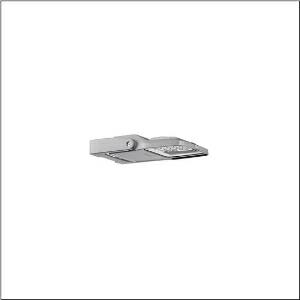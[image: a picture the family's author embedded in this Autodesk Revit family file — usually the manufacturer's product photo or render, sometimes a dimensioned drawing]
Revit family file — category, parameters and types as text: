
# Revit family: floodlight_fl_21_micro___pl52_5xa7761a4d2a_ddfa
name_source: partatom
category: Lighting Fixtures
units: mm (PartAtom-declared; Revit-internal decimal feet)

## family parameters
Cut with Voids When Loaded = No
Host = Face
Light Source = No
Part Type = Normal
Room Calculation Point = No
Round Connector Dimension = Use Diameter
Shared = No

## types (1)
- --- (1 x LED, 3010 lm, 23.1 W, 4000K)
    Apparent Load = 23 VA
    CIE Flux Codes = 26 60 98 100 100
    Color Rendering = 70
    Color Temperature = 4000K
    Default Elevation = 1800 mm
    Description = Floodlight FL 21 micro, floodlight, primary light control with lens, of PMMA, primary optical cover: protective disc, of toughened safety glass, transparent, light distribution: PL52, light emission: direct distribution, installation type: surface-mounted, LED, High Power LED, rated luminous flux: 3.010lm, luminous efficacy: 130lm/W, light colour: 740, colour temperature: 4000K, control gear: ECG iQ, control: optimised constant luminous flux control (CLO 2.0), Desk-Remote (wireless, voltage-free reading and setting of iQ features in the workshop via application-optimized NFC function/RFID function), Light-Fading, Smart-Wire, Night-Set, Lumen-Switch, Temp-Guard, Auto-Match, with terminal, 6-pole, mains connection: 220..240V, AC, 50/60Hz, start of lifetime: 23W, end of lifetime: 24W, reduction: 11W, luminaire housing, of diecast aluminium, powder-coated, Siteco® metallic grey (DB 702S), corrosivity category C5 according to DIN EN ISO 12944, design bracket, of diecast aluminium, powder-coated, Siteco® metallic grey (DB 702S), protection rating (complete): IP66, insulation class (complete): insulation class II (safety insulation), certification: CE, protection symbol: D, impact resistance: IK07, permissible operating ambient temperature: -40..+40°C, permissible operating ambient temperature for outdoor applications: -40..+50°C, standard: DIN EN 12944, packaging unit: 1 piece

Light Distribution: PL52
    Height = 65 mm
    Lamp = 1 x LED
    Lamp Light Flux = 3010 lm
    Lamp Power = 23.1 W
    Lamp count = 1
    Length = 312 mm
    Luminous efficacy = 130 lm/W
    Manufacturer = Siteco
    ModVariant = No
    Model = 5XA7761A4D2A
    Number of Poles = 1
    OnlyDefault = Yes
    Power Factor = 1
    Product Name = Floodlight FL 21 micro | PL52
    Product group = floodlight | pylon top
    ProductGroupID = 6101
    Protection Class = Protection class II
    Protection Degree = IP 66
    RLX_Detail_Level = 1
    RlxData = <blob elided: 97577 chars, md5=76b9c880>
    Socket = socket
    Standby Power = 0 W
    System Light Flux = 3010 lm
    System Power = 23 W
    Type Comments = factory setting: luminous flux: 100 % | dim-lin: 254 | 455 mA
    Type Image = l_1006878.jpg
    URL = http://relux.com
    VarID = @adj_090721
    Voltage = 0 V
    Weight = 0.00 kg
    Width = 230 mm

## geometry (parser evidence)
native form markers: Blend x4, Sweep x12
no freeform markers — native parametric forms only
